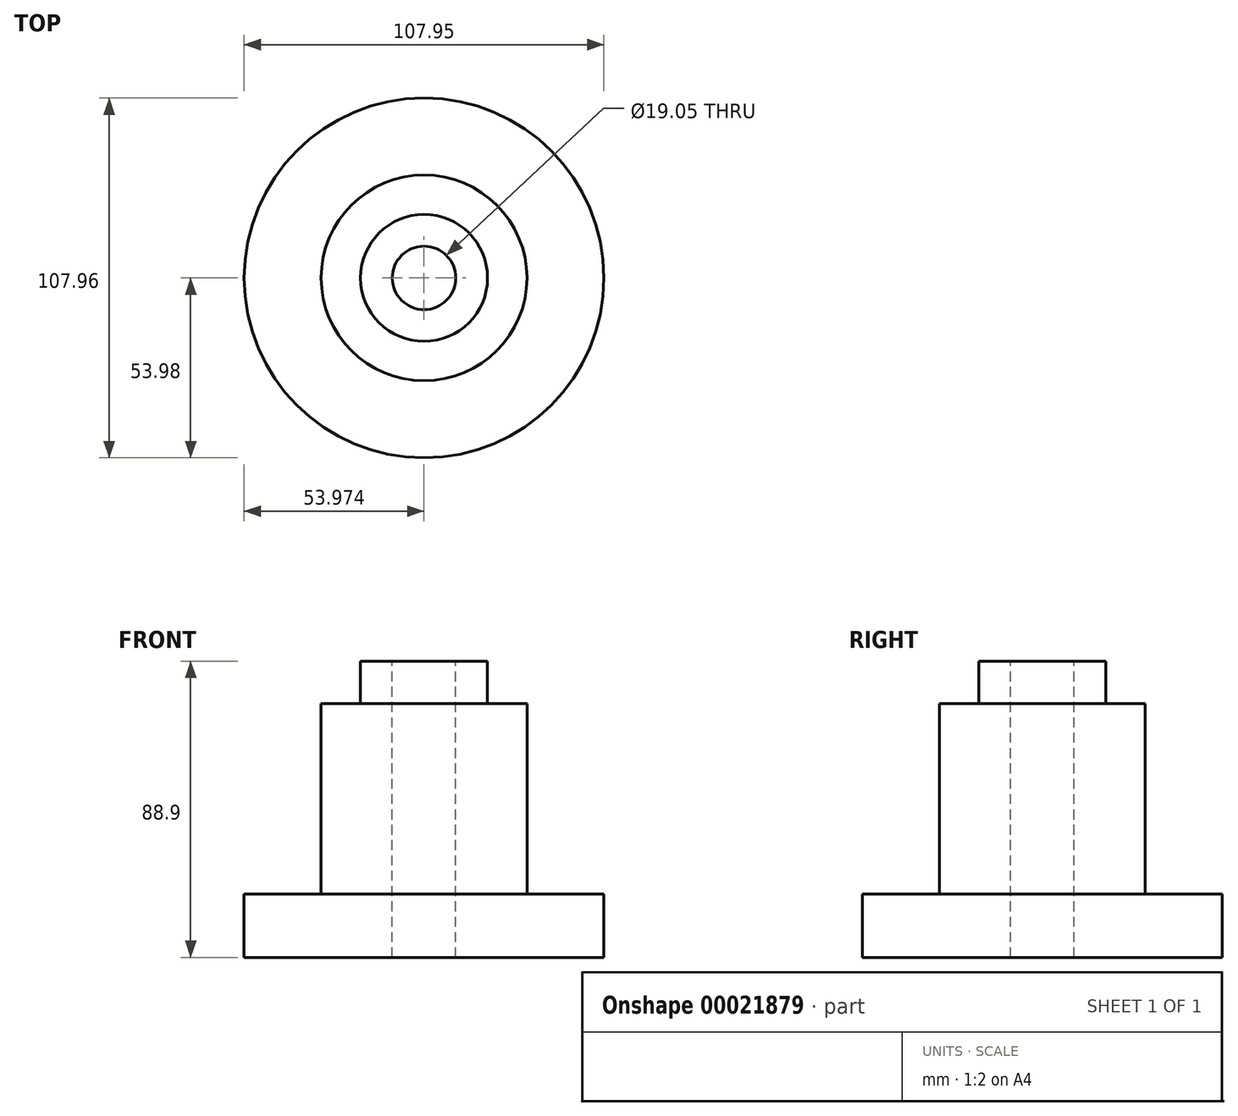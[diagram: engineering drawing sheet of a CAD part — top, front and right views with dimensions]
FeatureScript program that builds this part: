
annotation { "Feature Type Name" : "Feature", "Feature Type Description" : "" }
export const myFeature = defineFeature(function(context is Context, id is Id, definition is map)
    precondition{}
    {
        {
            var Q0;
            Q0=qCreatedBy(makeId("Front.planeOp"),FACE);
            var sketch = newSketch(context, id + "F0", { "sketchPlane" : qUnion([Q0])});
            skLineSegment(sketch, "E0", {"start": v(5.96, 28.32) * mm, "end": v(15.48, 28.32) * mm});
            skLineSegment(sketch, "E1", {"start": v(15.48, 28.32) * mm, "end": v(15.48, 15.62) * mm});
            skLineSegment(sketch, "E2", {"start": v(15.48, 15.62) * mm, "end": v(27.3, 15.62) * mm});
            skLineSegment(sketch, "E3", {"start": v(27.3, 15.62) * mm, "end": v(27.3, -41.53) * mm});
            skLineSegment(sketch, "E4", {"start": v(27.3, -41.53) * mm, "end": v(50.4, -41.53) * mm});
            skLineSegment(sketch, "E5", {"start": v(50.4, -41.53) * mm, "end": v(50.4, -60.58) * mm});
            skLineSegment(sketch, "E6", {"start": v(50.4, -60.58) * mm, "end": v(5.96, -60.58) * mm});
            skLineSegment(sketch, "E7", {"start": v(5.96, -60.58) * mm, "end": v(5.96, 28.32) * mm});
            skLineSegment(sketch, "E8", {"start": v(-3.57, 29.23) * mm, "end": v(-3.57, -60.87) * mm});
            skSolve(sketch);
        }
        {
            var Q0;
            Q0=makeQuery(id+"F0.imprint","IMPRINT",FACE,{"disambiguationData":[TD([[makeQuery(id+"F0.imprint","IMPRINT",EDGE,{"derivedFrom":sQuery(id+"F0.wireOp",EDGE,"E0")}),-1.0]])]});
            var Q1;
            Q1=sQuery(id+"F0.wireOp",EDGE,"E8");
            revolve(context, id + "F1", {"entities" : qUnion([Q0]), "axis" : qUnion([Q1]), "revolveType" : RevolveType.FULL});
        }
    });
